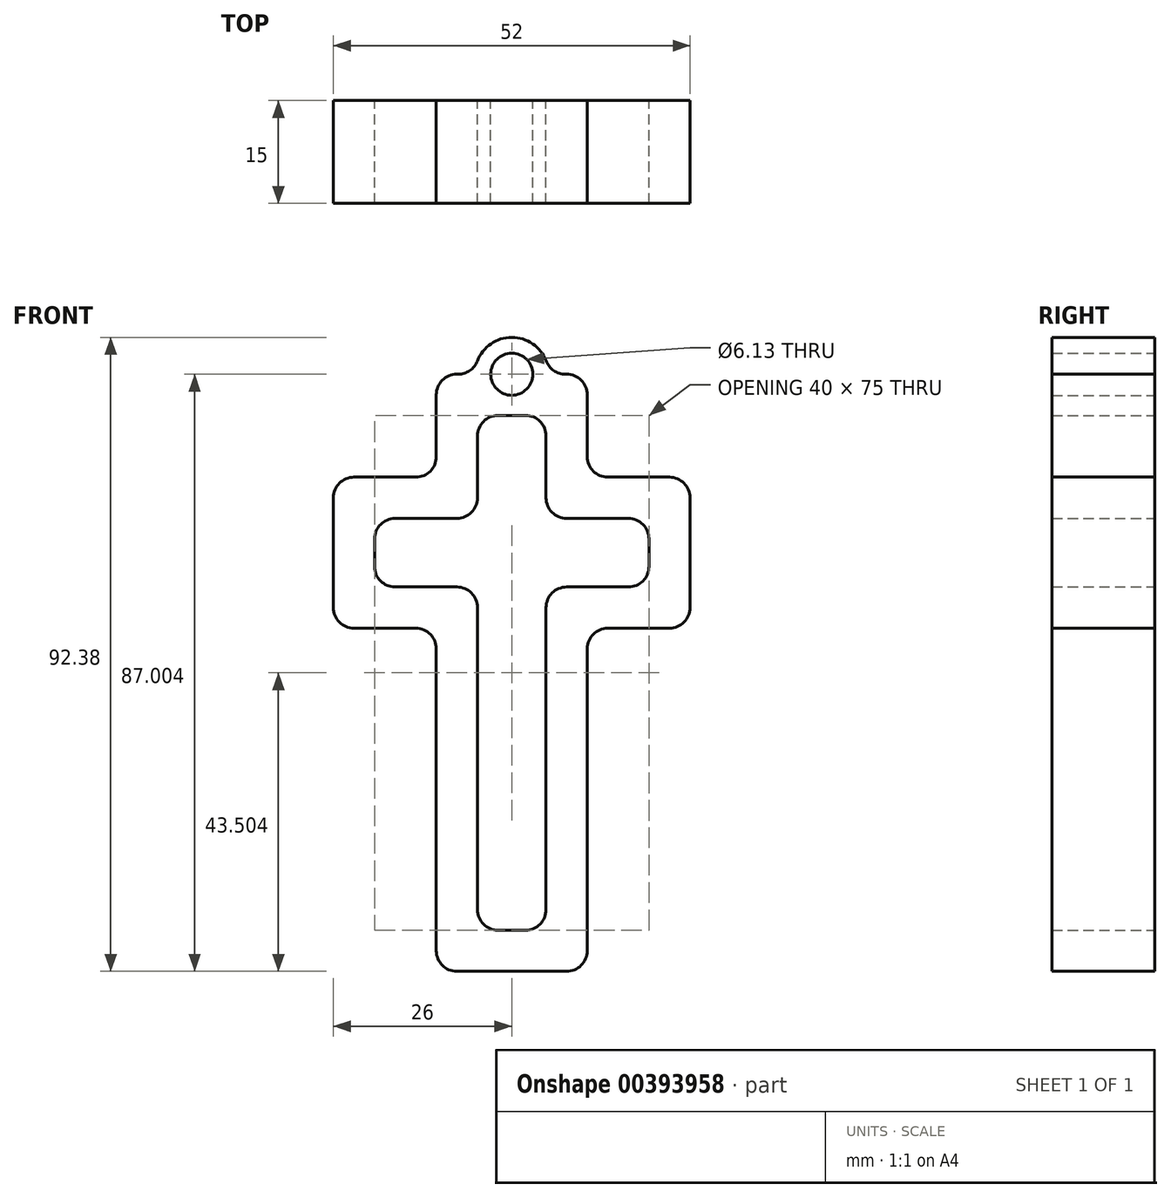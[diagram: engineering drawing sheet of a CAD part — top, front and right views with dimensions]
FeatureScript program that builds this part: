
annotation { "Feature Type Name" : "Feature", "Feature Type Description" : "" }
export const myFeature = defineFeature(function(context is Context, id is Id, definition is map)
    precondition{}
    {
        {
            var Q0;
            Q0=qCreatedBy(makeId("Front.planeOp"),FACE);
            var sketch = newSketch(context, id + "F0", { "sketchPlane" : qUnion([Q0])});
            skLineSegment(sketch, "E0", {"start": v(0, 58.13) * mm, "end": v(-10, 58.13) * mm});
            skLineSegment(sketch, "E1", {"start": v(-10, -16.87) * mm, "end": v(0, -16.87) * mm});
            skLineSegment(sketch, "E2", {"start": v(-10, 58.13) * mm, "end": v(-10, 43.13) * mm});
            skLineSegment(sketch, "E3", {"start": v(-10, 43.13) * mm, "end": v(-25, 43.13) * mm});
            skLineSegment(sketch, "E4", {"start": v(-25, 43.13) * mm, "end": v(-25, 33.13) * mm});
            skLineSegment(sketch, "E5", {"start": v(-25, 33.13) * mm, "end": v(-10, 33.13) * mm});
            skLineSegment(sketch, "E6", {"start": v(0, 43.13) * mm, "end": v(15, 43.13) * mm});
            skLineSegment(sketch, "E7", {"start": v(0, 33.13) * mm, "end": v(15, 33.13) * mm});
            skLineSegment(sketch, "E8", {"start": v(15, 43.13) * mm, "end": v(15, 33.13) * mm});
            skLineSegment(sketch, "E9", {"start": v(-10, 33.13) * mm, "end": v(-10, -16.87) * mm});
            skLineSegment(sketch, "E10", {"start": v(0, 58.13) * mm, "end": v(0, 43.13) * mm});
            skLineSegment(sketch, "E11", {"start": v(0, 33.13) * mm, "end": v(0, -16.87) * mm});
            skLineSegment(sketch, "E12", {"start": v(-16, -16.87) * mm, "end": v(-16, -22.87) * mm});
            skLineSegment(sketch, "E13", {"start": v(-16, -22.87) * mm, "end": v(6, -22.87) * mm});
            skLineSegment(sketch, "E14", {"start": v(-25, 27.13) * mm, "end": v(-16, 27.13) * mm});
            skLineSegment(sketch, "E15", {"start": v(-16, -16.87) * mm, "end": v(-16, 27.13) * mm});
            skLineSegment(sketch, "E16", {"start": v(6, -22.87) * mm, "end": v(6, 27.13) * mm});
            skLineSegment(sketch, "E17", {"start": v(6, 27.13) * mm, "end": v(15, 27.13) * mm});
            skLineSegment(sketch, "E18", {"start": v(15, 27.13) * mm, "end": v(21, 27.13) * mm});
            skLineSegment(sketch, "E19", {"start": v(21, 49.13) * mm, "end": v(6, 49.13) * mm});
            skLineSegment(sketch, "E20", {"start": v(6, 49.13) * mm, "end": v(6, 64.13) * mm});
            skLineSegment(sketch, "E21", {"start": v(6, 64.13) * mm, "end": v(-16, 64.13) * mm});
            skLineSegment(sketch, "E22", {"start": v(-16, 64.13) * mm, "end": v(-16, 49.13) * mm});
            skLineSegment(sketch, "E23", {"start": v(-16, 49.13) * mm, "end": v(-31, 49.13) * mm});
            skLineSegment(sketch, "E24", {"start": v(-31, 27.13) * mm, "end": v(-25, 27.13) * mm});
            skLineSegment(sketch, "E25", {"start": v(-16, 64.13) * mm, "end": v(-5, 64.13) * mm});
            skCircle(sketch, "E26", {"center": v(-5, 64.13) * mm, "radius": 5.37 * mm});
            skCircle(sketch, "E27", {"center": v(-5, 64.13) * mm, "radius": 3.07 * mm});
            skLineSegment(sketch, "E28", {"start": v(-5, 64.13) * mm, "end": v(-5, -22.87) * mm, "construction": true});
            skLineSegment(sketch, "E29", {"start": v(-31, 49.13) * mm, "end": v(-31, 27.13) * mm});
            skLineSegment(sketch, "E30", {"start": v(21, 49.13) * mm, "end": v(21, 27.13) * mm});
            skSolve(sketch);
        }
        {
            var Q0;
            Q0 = qSketchRegion(id + "F0", true);
            extrude(context, id + "F1", {"entities" : qUnion([Q0]), "depth" : 15 * mm});
        }
        {
            var Q0;
            Q0=makeQuery(id+"F1.opExtrude","SWEPT_EDGE",EDGE,{"disambiguationData":[OSD([sQuery(id+"F0.wireOp",EDGE,"E1"),sQuery(id+"F0.wireOp",EDGE,"E9"),sQuery(id+"F0.wireOp",EDGE,"SoNozwRW-mJtI-os8s-alWq-0gxmPMuzM5nE"),sQuery(id+"F0.wireOp",EDGE,"zj1N1qql-69xp-IFOC-AOg6-64gHm7Rjqr0n")])]});
            var Q1;
            Q1=makeQuery(id+"F1.opExtrude","SWEPT_EDGE",EDGE,{"disambiguationData":[OSD([sQuery(id+"F0.wireOp",EDGE,"E5"),sQuery(id+"F0.wireOp",EDGE,"E9")])]});
            var Q2;
            Q2=makeQuery(id+"F1.opExtrude","SWEPT_EDGE",EDGE,{"disambiguationData":[OSD([sQuery(id+"F0.wireOp",EDGE,"E4"),sQuery(id+"F0.wireOp",EDGE,"E5"),sQuery(id+"F0.wireOp",EDGE,"JkkYBlIC-WK7h-VhNU-eD4w-PFI7T7pZ055c")])]});
            var Q3;
            Q3=makeQuery(id+"F1.opExtrude","SWEPT_EDGE",EDGE,{"disambiguationData":[OSD([sQuery(id+"F0.wireOp",EDGE,"E1"),sQuery(id+"F0.wireOp",EDGE,"E11"),sQuery(id+"F0.wireOp",EDGE,"p5YPYbok-UCxx-zQt2-bGdL-7y8e1GDendUJ"),sQuery(id+"F0.wireOp",EDGE,"QCRdUmlX-UTfE-SmZh-7q9e-hv5Va6i25oJJ")])]});
            var Q4;
            Q4=makeQuery(id+"F1.opExtrude","SWEPT_EDGE",EDGE,{"disambiguationData":[OSD([sQuery(id+"F0.wireOp",EDGE,"E7"),sQuery(id+"F0.wireOp",EDGE,"E11")])]});
            var Q5;
            Q5=makeQuery(id+"F1.opExtrude","SWEPT_EDGE",EDGE,{"disambiguationData":[OSD([sQuery(id+"F0.wireOp",EDGE,"E7"),sQuery(id+"F0.wireOp",EDGE,"E8"),sQuery(id+"F0.wireOp",EDGE,"M5XVuVZv-HyxV-EBHI-0UWz-zm9aioapNkRY"),sQuery(id+"F0.wireOp",EDGE,"HJXAKwE1-8RYy-Ky9X-1OAD-b5Pzt5JmRXUv")])]});
            var Q6;
            Q6=makeQuery(id+"F1.opExtrude","SWEPT_EDGE",EDGE,{"disambiguationData":[OSD([sQuery(id+"F0.wireOp",EDGE,"E6"),sQuery(id+"F0.wireOp",EDGE,"E8"),sQuery(id+"F0.wireOp",EDGE,"t1L3Ds75-5ZQ1-6rzq-zuNa-BfBlgHZkFqex"),sQuery(id+"F0.wireOp",EDGE,"EY3CKX2p-qQSQ-HcfL-y7fS-CjnnHh3G8Awt")])]});
            var Q7;
            Q7=makeQuery(id+"F1.opExtrude","SWEPT_EDGE",EDGE,{"disambiguationData":[OSD([sQuery(id+"F0.wireOp",EDGE,"E6"),sQuery(id+"F0.wireOp",EDGE,"E10")])]});
            var Q8;
            Q8=makeQuery(id+"F1.opExtrude","SWEPT_EDGE",EDGE,{"disambiguationData":[OSD([sQuery(id+"F0.wireOp",EDGE,"E0"),sQuery(id+"F0.wireOp",EDGE,"E10")])]});
            var Q9;
            Q9=makeQuery(id+"F1.opExtrude","SWEPT_EDGE",EDGE,{"disambiguationData":[OSD([sQuery(id+"F0.wireOp",EDGE,"E0"),sQuery(id+"F0.wireOp",EDGE,"E2")])]});
            var Q10;
            Q10=makeQuery(id+"F1.opExtrude","SWEPT_EDGE",EDGE,{"disambiguationData":[OSD([sQuery(id+"F0.wireOp",EDGE,"E2"),sQuery(id+"F0.wireOp",EDGE,"E3")])]});
            var Q11;
            Q11=makeQuery(id+"F1.opExtrude","SWEPT_EDGE",EDGE,{"disambiguationData":[OSD([sQuery(id+"F0.wireOp",EDGE,"E3"),sQuery(id+"F0.wireOp",EDGE,"E4")])]});
            fillet(context, id + "F2", {"entities" : qUnion([Q0, Q1, Q2, Q3, Q4, Q5, Q6, Q7, Q8, Q9, Q10, Q11]), "radius" : 3 * mm, "tangentPropagation" : true, "allowEdgeOverflow" : false});
        }
        {
            var Q0;
            Q0=makeQuery(id+"F1.opExtrude","SWEPT_EDGE",EDGE,{"disambiguationData":[OSD([sQuery(id+"F0.wireOp",EDGE,"E19"),sQuery(id+"F0.wireOp",EDGE,"E20")])]});
            fillet(context, id + "F3", {"entities" : qUnion([Q0]), "radius" : 3 * mm, "tangentPropagation" : true, "allowEdgeOverflow" : false});
        }
        {
            var Q0;
            Q0=makeQuery(id+"F1.opExtrude","SWEPT_EDGE",EDGE,{"disambiguationData":[OSD([sQuery(id+"F0.wireOp",EDGE,"E20"),sQuery(id+"F0.wireOp",EDGE,"E21")])]});
            var Q1;
            Q1=makeQuery(id+"F1.opExtrude","SWEPT_EDGE",EDGE,{"disambiguationData":[OSD([sQuery(id+"F0.wireOp",EDGE,"E21"),sQuery(id+"F0.wireOp",EDGE,"E26")])]});
            var Q2;
            Q2=makeQuery(id+"F1.opExtrude","SWEPT_EDGE",EDGE,{"disambiguationData":[OSD([sQuery(id+"F0.wireOp",EDGE,"sMuBDEL5-hzGn-YPGm-qX1Y-40NOGYWRmCt9"),sQuery(id+"F0.wireOp",EDGE,"E19")])]});
            var Q3;
            Q3=makeQuery(id+"F1.opExtrude","SWEPT_EDGE",EDGE,{"disambiguationData":[OSD([sQuery(id+"F0.wireOp",EDGE,"E18"),sQuery(id+"F0.wireOp",EDGE,"sMuBDEL5-hzGn-YPGm-qX1Y-40NOGYWRmCt9")])]});
            var Q4;
            Q4=makeQuery(id+"F1.opExtrude","SWEPT_EDGE",EDGE,{"disambiguationData":[OSD([sQuery(id+"F0.wireOp",EDGE,"E16"),sQuery(id+"F0.wireOp",EDGE,"E17")])]});
            var Q5;
            Q5=makeQuery(id+"F1.opExtrude","SWEPT_EDGE",EDGE,{"disambiguationData":[OSD([sQuery(id+"F0.wireOp",EDGE,"E13"),sQuery(id+"F0.wireOp",EDGE,"E16")])]});
            var Q6;
            Q6=makeQuery(id+"F1.opExtrude","SWEPT_EDGE",EDGE,{"disambiguationData":[OSD([sQuery(id+"F0.wireOp",EDGE,"E12"),sQuery(id+"F0.wireOp",EDGE,"E13")])]});
            var Q7;
            Q7=makeQuery(id+"F1.opExtrude","SWEPT_EDGE",EDGE,{"disambiguationData":[OSD([sQuery(id+"F0.wireOp",EDGE,"E14"),sQuery(id+"F0.wireOp",EDGE,"E15")])]});
            var Q8;
            Q8=makeQuery(id+"F1.opExtrude","SWEPT_EDGE",EDGE,{"disambiguationData":[OSD([sQuery(id+"F0.wireOp",EDGE,"2tCYhLwo-kV1n-wEjR-YmM0-9tpOZI8bn5kh"),sQuery(id+"F0.wireOp",EDGE,"E24")])]});
            var Q9;
            Q9=makeQuery(id+"F1.opExtrude","SWEPT_EDGE",EDGE,{"disambiguationData":[OSD([sQuery(id+"F0.wireOp",EDGE,"E23"),sQuery(id+"F0.wireOp",EDGE,"2tCYhLwo-kV1n-wEjR-YmM0-9tpOZI8bn5kh")])]});
            var Q10;
            Q10=makeQuery(id+"F1.opExtrude","SWEPT_EDGE",EDGE,{"disambiguationData":[OSD([sQuery(id+"F0.wireOp",EDGE,"E25"),sQuery(id+"F0.wireOp",EDGE,"E26")])]});
            var Q11;
            Q11=makeQuery(id+"F1.opExtrude","SWEPT_EDGE",EDGE,{"disambiguationData":[OSD([sQuery(id+"F0.wireOp",EDGE,"E22"),sQuery(id+"F0.wireOp",EDGE,"E25")])]});
            var Q12;
            Q12=makeQuery(id+"F1.opExtrude","SWEPT_EDGE",EDGE,{"disambiguationData":[OSD([sQuery(id+"F0.wireOp",EDGE,"E22"),sQuery(id+"F0.wireOp",EDGE,"E23")])]});
            fillet(context, id + "F4", {"entities" : qUnion([Q0, Q1, Q2, Q3, Q4, Q5, Q6, Q7, Q8, Q9, Q10, Q11, Q12]), "radius" : 3 * mm, "tangentPropagation" : true, "allowEdgeOverflow" : false});
        }
    });
